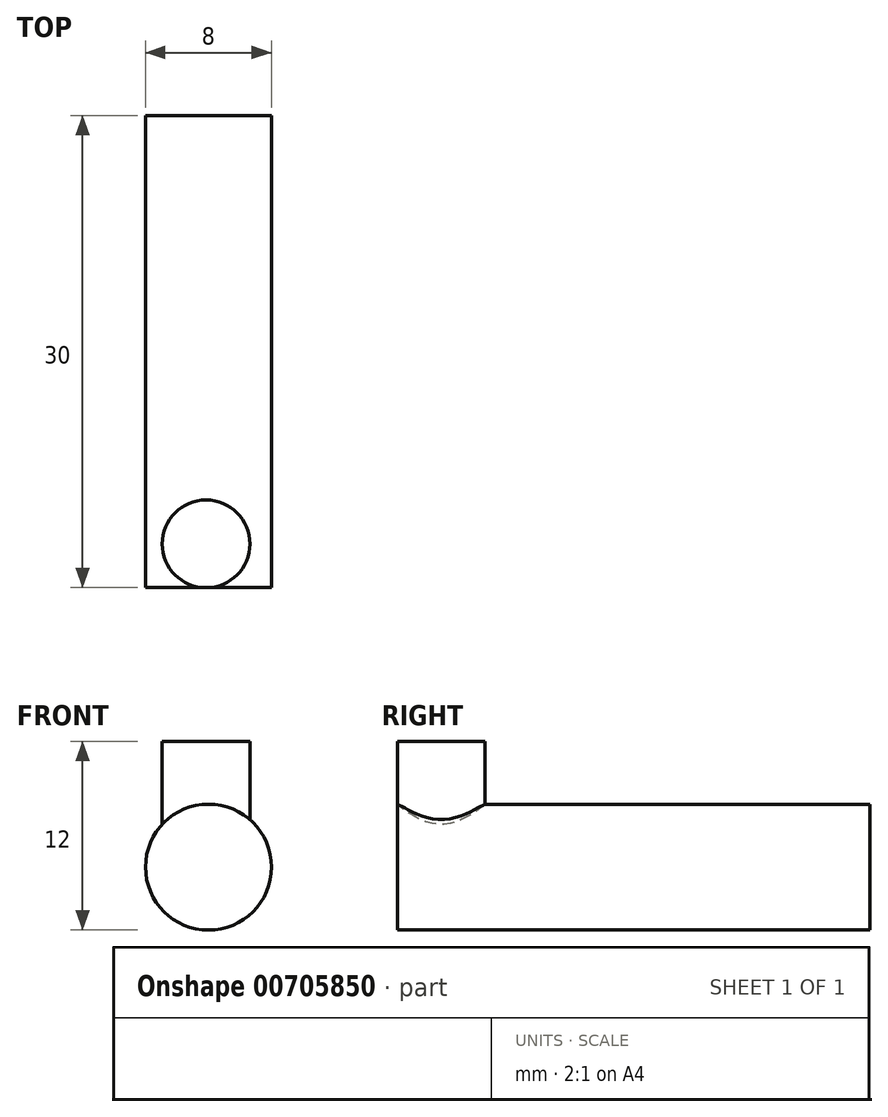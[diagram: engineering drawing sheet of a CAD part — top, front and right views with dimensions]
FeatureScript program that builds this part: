
annotation { "Feature Type Name" : "Feature", "Feature Type Description" : "" }
export const myFeature = defineFeature(function(context is Context, id is Id, definition is map)
    precondition{}
    {
        {
            var Q0;
            Q0=qCreatedBy(makeId("Front.planeOp"),FACE);
            var sketch = newSketch(context, id + "F0", { "sketchPlane" : qUnion([Q0])});
            skCircle(sketch, "E0", {"center": v(-24.13, 23.67) * mm, "radius": 4 * mm});
            skSolve(sketch);
        }
        {
            var Q0;
            Q0=makeQuery(id+"F0.imprint","IMPRINT",FACE,{"disambiguationData":[TD([[makeQuery(id+"F0.imprint","IMPRINT",EDGE,{"derivedFrom":sQuery(id+"F0.wireOp",EDGE,"E0")}),1.0]])]});
            extrude(context, id + "F1", {"entities" : qUnion([Q0]), "depth" : 30 * mm, "offsetDistance" : 25 * mm});
        }
        {
            var Q0;
            Q0=makeQuery(id+"F1.opExtrude","SWEPT_FACE",FACE,{"disambiguationData":[OSD([sQuery(id+"F0.wireOp",EDGE,"E0")])]});
            cPlane(context, id + "F2", {"entities" : qUnion([Q0]), "cplaneType" : CPlaneType.LINE_ANGLE, "offset" : 25 * mm, "angle" : 0 * degree, "width" : 150 * mm, "height" : 150 * mm});
        }
        {
            var Q0;
            Q0=qCreatedBy(id+"F2.planeOp",FACE);
            var sketch = newSketch(context, id + "F3", { "sketchPlane" : qUnion([Q0])});
            skCircle(sketch, "E1", {"center": v(-24.28, -27.21) * mm, "radius": 2.79 * mm});
            skSolve(sketch);
        }
        {
            var Q0;
            Q0 = qSketchRegion(id + "F3", true);
            extrude(context, id + "F4", {"entities" : qUnion([Q0]), "operationType" : NewBodyOperationType.ADD, "depth" : 8 * mm, "offsetDistance" : 25 * mm});
        }
    });
